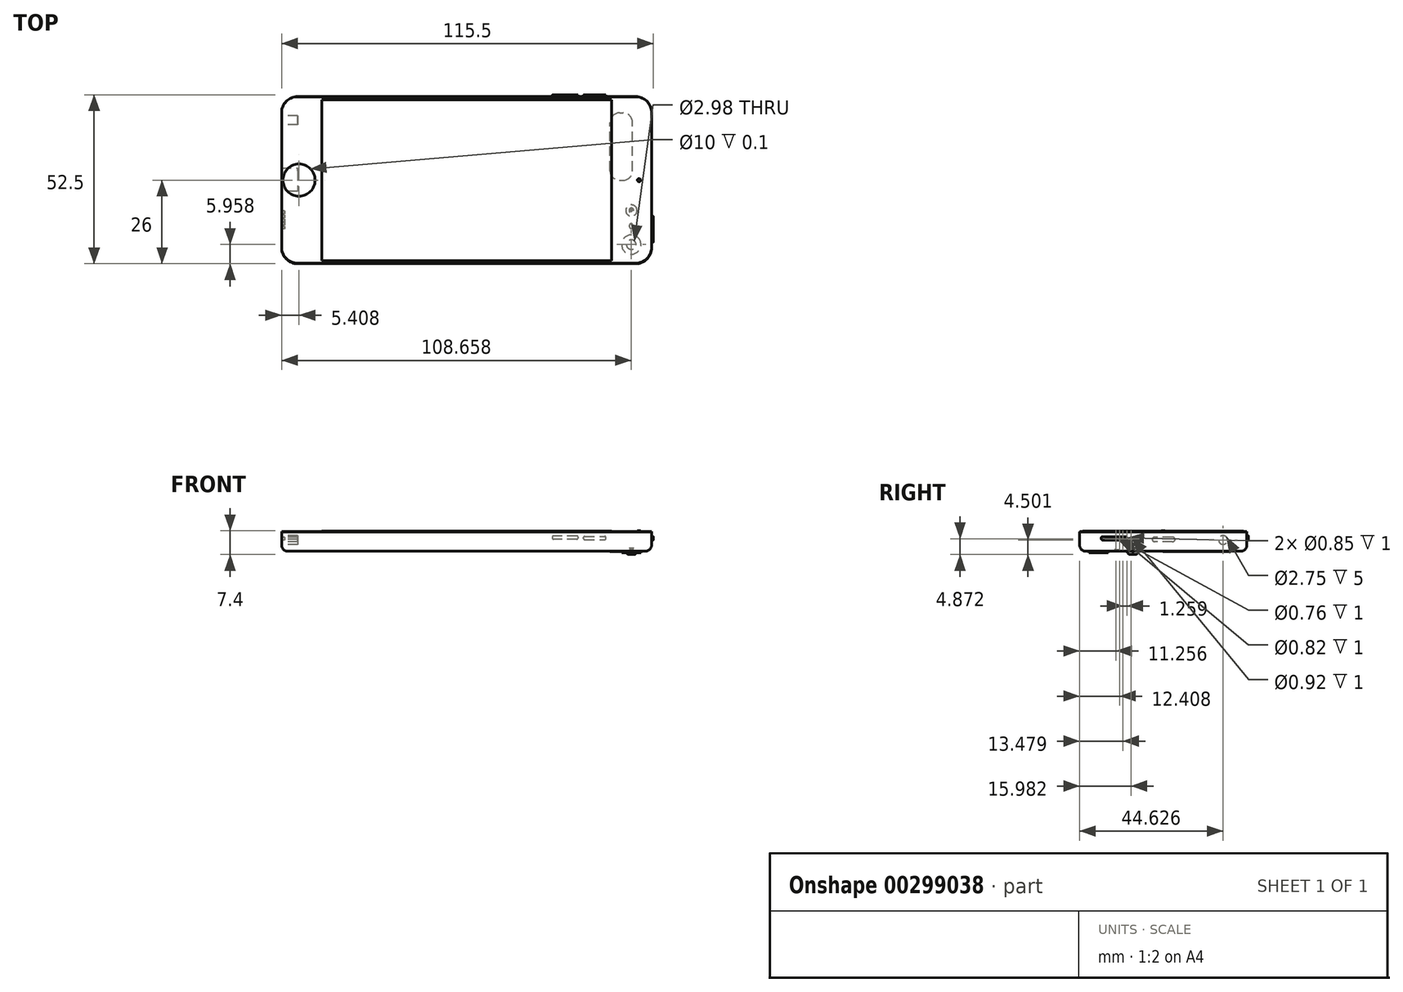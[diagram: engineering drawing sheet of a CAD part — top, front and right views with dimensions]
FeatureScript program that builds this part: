
annotation { "Feature Type Name" : "Feature", "Feature Type Description" : "" }
export const myFeature = defineFeature(function(context is Context, id is Id, definition is map)
    precondition{}
    {
        {
            var Q0;
            Q0=qCreatedBy(makeId("Top.planeOp"),FACE);
            var sketch = newSketch(context, id + "F0", { "sketchPlane" : qUnion([Q0])});
            skLineSegment(sketch, "E0.rect.bottom", {"start": v(-57.5, 26) * mm, "end": v(57.5, 26) * mm});
            skLineSegment(sketch, "E0.rect.top", {"start": v(-57.5, -26) * mm, "end": v(57.5, -26) * mm});
            skLineSegment(sketch, "E0.rect.left", {"start": v(-57.5, 26) * mm, "end": v(-57.5, -26) * mm});
            skLineSegment(sketch, "E0.rect.right", {"start": v(57.5, 26) * mm, "end": v(57.5, -26) * mm});
            skPoint(sketch, "E0.rect.middle", {"position": v(0, 0) * mm});
            skSolve(sketch);
        }
        {
            var Q0;
            Q0=makeQuery(id+"F0.imprint","IMPRINT",FACE,{"disambiguationData":[TD([[makeQuery(id+"F0.imprint","IMPRINT",EDGE,{"derivedFrom":sQuery(id+"F0.wireOp",EDGE,"E0.rect.bottom")}),-1.0]])]});
            extrude(context, id + "F1", {"entities" : qUnion([Q0]), "depth" : 6 * mm});
        }
        {
            var Q0;
            Q0=makeQuery(id+"F1.opExtrude","SWEPT_EDGE",EDGE,{"disambiguationData":[OSD([sQuery(id+"F0.wireOp",EDGE,"E0.rect.bottom"),sQuery(id+"F0.wireOp",EDGE,"E0.rect.right")])]});
            fillet(context, id + "F2", {"entities" : qUnion([Q0]), "radius" : 5 * mm, "tangentPropagation" : true, "allowEdgeOverflow" : false});
        }
        {
            var Q0;
            Q0=makeQuery(id+"F1.opExtrude","SWEPT_EDGE",EDGE,{"disambiguationData":[OSD([sQuery(id+"F0.wireOp",EDGE,"E0.rect.top"),sQuery(id+"F0.wireOp",EDGE,"E0.rect.right")])]});
            fillet(context, id + "F3", {"entities" : qUnion([Q0]), "radius" : 5 * mm, "tangentPropagation" : true, "allowEdgeOverflow" : false});
        }
        {
            var Q0;
            Q0=makeQuery(id+"F1.opExtrude","SWEPT_EDGE",EDGE,{"disambiguationData":[OSD([sQuery(id+"F0.wireOp",EDGE,"E0.rect.top"),sQuery(id+"F0.wireOp",EDGE,"E0.rect.left")])]});
            fillet(context, id + "F4", {"entities" : qUnion([Q0]), "radius" : 5 * mm, "tangentPropagation" : true, "allowEdgeOverflow" : false});
        }
        {
            var Q0;
            Q0=makeQuery(id+"F1.opExtrude","SWEPT_EDGE",EDGE,{"disambiguationData":[OSD([sQuery(id+"F0.wireOp",EDGE,"E0.rect.bottom"),sQuery(id+"F0.wireOp",EDGE,"E0.rect.left")])]});
            fillet(context, id + "F5", {"entities" : qUnion([Q0]), "radius" : 5 * mm, "tangentPropagation" : true, "allowEdgeOverflow" : false});
        }
        {
            var Q0;
            Q0=makeQuery(id+"F1.opExtrude","CAP_EDGE",EDGE,{"disambiguationData":[OSD([sQuery(id+"F0.wireOp",EDGE,"E0.rect.top")])],"isStart":true});
            fillet(context, id + "F6", {"entities" : qUnion([Q0]), "radius" : 2 * mm, "tangentPropagation" : true, "allowEdgeOverflow" : false});
        }
        {
            var Q0;
            Q0=makeQuery(id+"F1.opExtrude","SWEPT_FACE",FACE,{"disambiguationData":[OSD([sQuery(id+"F0.wireOp",EDGE,"E0.rect.bottom")])]});
            var sketch = newSketch(context, id + "F7", { "sketchPlane" : qUnion([Q0])});
            skLineSegment(sketch, "E1.right", {"start": v(-43.3, 3.62) * mm, "end": v(-43.3, 4.62) * mm});
            skLineSegment(sketch, "E2.0.MirrorCS", {"start": v(-36.3, 4.62) * mm, "end": v(-43.3, 4.62) * mm});
            skLineSegment(sketch, "E3.0.MirrorCS", {"start": v(-36.3, 3.62) * mm, "end": v(-36.3, 4.62) * mm});
            skLineSegment(sketch, "E4.0.MirrorCS", {"start": v(-36.3, 3.62) * mm, "end": v(-43.3, 3.62) * mm});
            skSolve(sketch);
        }
        {
            var Q0;
            Q0=qSketchRegion(id+"F7",true);
            extrude(context, id + "F8", {"entities" : qUnion([Q0]), "operationType" : NewBodyOperationType.ADD, "depth" : .5 * mm});
        }
        {
            var Q0;
            Q0=makeQuery(id+"F8.opExtrude","SWEPT_EDGE",EDGE,{"disambiguationData":[OSD([sQuery(id+"F7.wireOp",EDGE,"E1.right"),sQuery(id+"F7.wireOp",EDGE,"E2.0.MirrorCS")])]});
            var Q1;
            Q1=makeQuery(id+"F8.opExtrude","SWEPT_EDGE",EDGE,{"disambiguationData":[OSD([sQuery(id+"F7.wireOp",EDGE,"E1.right"),sQuery(id+"F7.wireOp",EDGE,"E4.0.MirrorCS")])]});
            var Q2;
            Q2=makeQuery(id+"F8.opExtrude","SWEPT_EDGE",EDGE,{"disambiguationData":[OSD([sQuery(id+"F7.wireOp",EDGE,"E3.0.MirrorCS"),sQuery(id+"F7.wireOp",EDGE,"E4.0.MirrorCS")])]});
            var Q3;
            Q3=makeQuery(id+"F8.opExtrude","SWEPT_EDGE",EDGE,{"disambiguationData":[OSD([sQuery(id+"F7.wireOp",EDGE,"E2.0.MirrorCS"),sQuery(id+"F7.wireOp",EDGE,"E3.0.MirrorCS")])]});
            fillet(context, id + "F9", {"entities" : qUnion([Q0, Q1, Q2, Q3]), "radius" : .4 * mm, "tangentPropagation" : true, "allowEdgeOverflow" : false});
        }
        {
            var Q0;
            Q0=makeQuery(id+"F1.opExtrude","SWEPT_FACE",FACE,{"disambiguationData":[OSD([sQuery(id+"F0.wireOp",EDGE,"E0.rect.bottom")])]});
            var sketch = newSketch(context, id + "F10", { "sketchPlane" : qUnion([Q0])});
            skLineSegment(sketch, "E5.bottom", {"start": v(-34.62, 4.76) * mm, "end": v(-26.62, 4.76) * mm});
            skLineSegment(sketch, "E5.top", {"start": v(-34.62, 3.76) * mm, "end": v(-26.62, 3.76) * mm});
            skLineSegment(sketch, "E5.left", {"start": v(-34.62, 4.76) * mm, "end": v(-34.62, 3.76) * mm});
            skLineSegment(sketch, "E5.right", {"start": v(-26.62, 4.76) * mm, "end": v(-26.62, 3.76) * mm});
            skSolve(sketch);
        }
        {
            var Q0;
            Q0=qSketchRegion(id+"F10",true);
            extrude(context, id + "F11", {"entities" : qUnion([Q0]), "operationType" : NewBodyOperationType.ADD, "depth" : .5 * mm});
        }
        {
            var Q0;
            Q0=makeQuery(id+"F11.opExtrude","SWEPT_EDGE",EDGE,{"disambiguationData":[OSD([sQuery(id+"F10.wireOp",EDGE,"E5.bottom"),sQuery(id+"F10.wireOp",EDGE,"E5.left")])]});
            var Q1;
            Q1=makeQuery(id+"F11.opExtrude","SWEPT_EDGE",EDGE,{"disambiguationData":[OSD([sQuery(id+"F10.wireOp",EDGE,"E5.top"),sQuery(id+"F10.wireOp",EDGE,"E5.left")])]});
            var Q2;
            Q2=makeQuery(id+"F11.opExtrude","SWEPT_EDGE",EDGE,{"disambiguationData":[OSD([sQuery(id+"F10.wireOp",EDGE,"E5.top"),sQuery(id+"F10.wireOp",EDGE,"E5.right")])]});
            var Q3;
            Q3=makeQuery(id+"F11.opExtrude","SWEPT_EDGE",EDGE,{"disambiguationData":[OSD([sQuery(id+"F10.wireOp",EDGE,"E5.bottom"),sQuery(id+"F10.wireOp",EDGE,"E5.right")])]});
            fillet(context, id + "F12", {"entities" : qUnion([Q0, Q1, Q2, Q3]), "radius" : .4 * mm, "tangentPropagation" : true, "allowEdgeOverflow" : false});
        }
        {
            var Q0;
            Q0=makeQuery(id+"F1.opExtrude","SWEPT_FACE",FACE,{"disambiguationData":[OSD([sQuery(id+"F0.wireOp",EDGE,"E0.rect.left")])]});
            var sketch = newSketch(context, id + "F13", { "sketchPlane" : qUnion([Q0])});
            skCircle(sketch, "E6", {"center": v(-18.63, 3.5) * mm, "radius": 1.38 * mm});
            skSolve(sketch);
        }
        {
            var Q0;
            Q0=qSketchRegion(id+"F13",true);
            extrude(context, id + "F14", {"entities" : qUnion([Q0]), "operationType" : NewBodyOperationType.REMOVE, "oppositeDirection" : true, "depth" : 5 * mm});
        }
        {
            var Q0;
            Q0=makeQuery(id+"F1.opExtrude","SWEPT_FACE",FACE,{"disambiguationData":[OSD([sQuery(id+"F0.wireOp",EDGE,"E0.rect.left")])]});
            var sketch = newSketch(context, id + "F15", { "sketchPlane" : qUnion([Q0])});
            skLineSegment(sketch, "E7.bottom", {"start": v(-3.75, 4.39) * mm, "end": v(3.47, 4.39) * mm});
            skLineSegment(sketch, "E7.top", {"start": v(-3.75, 2.97) * mm, "end": v(3.47, 2.97) * mm});
            skLineSegment(sketch, "E7.left", {"start": v(-3.75, 4.39) * mm, "end": v(-3.75, 2.97) * mm});
            skLineSegment(sketch, "E7.right", {"start": v(3.47, 4.39) * mm, "end": v(3.47, 2.97) * mm});
            skSolve(sketch);
        }
        {
            var Q0;
            Q0=makeQuery(id+"F15.imprint","IMPRINT",FACE,{"disambiguationData":[TD([[makeQuery(id+"F15.imprint","IMPRINT",EDGE,{"derivedFrom":sQuery(id+"F15.wireOp",EDGE,"E7.bottom")}),-1.0]])]});
            extrude(context, id + "F16", {"entities" : qUnion([Q0]), "operationType" : NewBodyOperationType.REMOVE, "oppositeDirection" : true, "depth" : 5 * mm});
        }
        {
            var Q0;
            Q0=makeQuery(id+"F16.boolean.opBoolean","COPY",EDGE,{"derivedFrom":makeQuery(id+"F16.opExtrude","SWEPT_EDGE",EDGE,{"disambiguationData":[OSD([sQuery(id+"F15.wireOp",EDGE,"E7.bottom"),sQuery(id+"F15.wireOp",EDGE,"E7.left")])]})});
            var Q1;
            Q1=makeQuery(id+"F16.boolean.opBoolean","COPY",EDGE,{"derivedFrom":makeQuery(id+"F16.opExtrude","SWEPT_EDGE",EDGE,{"disambiguationData":[OSD([sQuery(id+"F15.wireOp",EDGE,"E7.top"),sQuery(id+"F15.wireOp",EDGE,"E7.left")])]})});
            var Q2;
            Q2=makeQuery(id+"F16.boolean.opBoolean","COPY",EDGE,{"derivedFrom":makeQuery(id+"F16.opExtrude","SWEPT_EDGE",EDGE,{"disambiguationData":[OSD([sQuery(id+"F15.wireOp",EDGE,"E7.bottom"),sQuery(id+"F15.wireOp",EDGE,"E7.right")])]})});
            var Q3;
            Q3=makeQuery(id+"F16.boolean.opBoolean","COPY",EDGE,{"derivedFrom":makeQuery(id+"F16.opExtrude","SWEPT_EDGE",EDGE,{"disambiguationData":[OSD([sQuery(id+"F15.wireOp",EDGE,"E7.top"),sQuery(id+"F15.wireOp",EDGE,"E7.right")])]})});
            fillet(context, id + "F17", {"entities" : qUnion([Q0, Q1, Q2, Q3]), "radius" : .9 * mm, "tangentPropagation" : true, "allowEdgeOverflow" : false});
        }
        {
            var Q0;
            Q0=makeQuery(id+"F1.opExtrude","SWEPT_FACE",FACE,{"disambiguationData":[OSD([sQuery(id+"F0.wireOp",EDGE,"E0.rect.left")])]});
            var sketch = newSketch(context, id + "F18", { "sketchPlane" : qUnion([Q0])});
            skCircle(sketch, "E8", {"center": v(10.02, 3.87) * mm, "radius": 0.46 * mm});
            skCircle(sketch, "E9", {"center": v(11.26, 3.87) * mm, "radius": 0.42 * mm});
            skCircle(sketch, "E10", {"center": v(12.52, 3.87) * mm, "radius": 0.42 * mm});
            skCircle(sketch, "E11", {"center": v(13.6, 3.87) * mm, "radius": 0.41 * mm});
            skCircle(sketch, "E12", {"center": v(14.74, 3.87) * mm, "radius": 0.38 * mm});
            skSolve(sketch);
        }
        {
            var Q0;
            Q0=qSketchRegion(id+"F18",true);
            extrude(context, id + "F19", {"entities" : qUnion([Q0]), "operationType" : NewBodyOperationType.REMOVE, "oppositeDirection" : true, "depth" : 1 * mm});
        }
        {
            var Q0;
            Q0=makeQuery(id+"F1.opExtrude","SWEPT_FACE",FACE,{"disambiguationData":[OSD([sQuery(id+"F0.wireOp",EDGE,"E0.rect.right")])]});
            var sketch = newSketch(context, id + "F20", { "sketchPlane" : qUnion([Q0])});
            skLineSegment(sketch, "E13.bottom", {"start": v(-19.26, 4.51) * mm, "end": v(-11.26, 4.51) * mm});
            skLineSegment(sketch, "E13.top", {"start": v(-19.26, 3.51) * mm, "end": v(-11.26, 3.51) * mm});
            skLineSegment(sketch, "E13.left", {"start": v(-19.26, 4.51) * mm, "end": v(-19.26, 3.51) * mm});
            skLineSegment(sketch, "E13.right", {"start": v(-11.26, 4.51) * mm, "end": v(-11.26, 3.51) * mm});
            skSolve(sketch);
        }
        {
            var Q0;
            Q0=makeQuery(id+"F20.imprint","IMPRINT",FACE,{"disambiguationData":[TD([[makeQuery(id+"F20.imprint","IMPRINT",EDGE,{"derivedFrom":sQuery(id+"F20.wireOp",EDGE,"E13.bottom")}),-1.0]])]});
            extrude(context, id + "F21", {"entities" : qUnion([Q0]), "operationType" : NewBodyOperationType.ADD, "depth" : .5 * mm});
        }
        {
            var Q0;
            Q0=makeQuery(id+"F21.opExtrude","SWEPT_EDGE",EDGE,{"disambiguationData":[OSD([sQuery(id+"F20.wireOp",EDGE,"E13.bottom"),sQuery(id+"F20.wireOp",EDGE,"E13.left")])]});
            var Q1;
            Q1=makeQuery(id+"F21.opExtrude","SWEPT_EDGE",EDGE,{"disambiguationData":[OSD([sQuery(id+"F20.wireOp",EDGE,"E13.top"),sQuery(id+"F20.wireOp",EDGE,"E13.left")])]});
            var Q2;
            Q2=makeQuery(id+"F21.opExtrude","SWEPT_EDGE",EDGE,{"disambiguationData":[OSD([sQuery(id+"F20.wireOp",EDGE,"E13.bottom"),sQuery(id+"F20.wireOp",EDGE,"E13.right")])]});
            var Q3;
            Q3=makeQuery(id+"F21.opExtrude","SWEPT_EDGE",EDGE,{"disambiguationData":[OSD([sQuery(id+"F20.wireOp",EDGE,"E13.top"),sQuery(id+"F20.wireOp",EDGE,"E13.right")])]});
            fillet(context, id + "F22", {"entities" : qUnion([Q0, Q1, Q2, Q3]), "radius" : .4 * mm, "tangentPropagation" : true, "allowEdgeOverflow" : false});
        }
        {
            var Q0;
            Q0=makeQuery(id+"F1.opExtrude","CAP_FACE",FACE,{"disambiguationData":[OSD([sQuery(id+"F0.wireOp",EDGE,"E0.rect.bottom"),sQuery(id+"F0.wireOp",EDGE,"E0.rect.top"),sQuery(id+"F0.wireOp",EDGE,"E0.rect.left"),sQuery(id+"F0.wireOp",EDGE,"E0.rect.right")])],"isStart":true});
            var sketch = newSketch(context, id + "F23", { "sketchPlane" : qUnion([Q0])});
            skCircle(sketch, "E14", {"center": v(51.16, 20.04) * mm, "radius": 3 * mm});
            skCircle(sketch, "E15", {"center": v(51.16, 20.04) * mm, "radius": 1.5 * mm});
            skSolve(sketch);
        }
        {
            var Q0;
            Q0=makeQuery(id+"F23.imprint","IMPRINT",FACE,{"disambiguationData":[TD([[makeQuery(id+"F23.imprint","IMPRINT",EDGE,{"derivedFrom":sQuery(id+"F23.wireOp",EDGE,"E14")}),1.0]])]});
            extrude(context, id + "F24", {"entities" : qUnion([Q0]), "depth" : .5 * mm});
        }
        {
            var Q0;
            Q0=makeQuery(id+"F1.opExtrude","CAP_FACE",FACE,{"disambiguationData":[OSD([sQuery(id+"F0.wireOp",EDGE,"E0.rect.bottom"),sQuery(id+"F0.wireOp",EDGE,"E0.rect.top"),sQuery(id+"F0.wireOp",EDGE,"E0.rect.left"),sQuery(id+"F0.wireOp",EDGE,"E0.rect.right")])],"isStart":true});
            var sketch = newSketch(context, id + "F25", { "sketchPlane" : qUnion([Q0])});
            skLineSegment(sketch, "E16.rect.bottom", {"start": v(50.61, 15.04) * mm, "end": v(51.61, 15.04) * mm});
            skLineSegment(sketch, "E16.rect.top", {"start": v(50.61, 13.54) * mm, "end": v(51.61, 13.54) * mm});
            skLineSegment(sketch, "E16.rect.left", {"start": v(50.61, 15.04) * mm, "end": v(50.61, 13.54) * mm});
            skLineSegment(sketch, "E16.rect.right", {"start": v(51.61, 15.04) * mm, "end": v(51.61, 13.54) * mm});
            skPoint(sketch, "E16.rect.middle", {"position": v(51.11, 14.3) * mm});
            skSolve(sketch);
        }
        {
            var Q0;
            Q0=qSketchRegion(id+"F25",true);
            extrude(context, id + "F26", {"entities" : qUnion([Q0]), "operationType" : NewBodyOperationType.REMOVE, "oppositeDirection" : true, "depth" : .5 * mm});
        }
        {
            var Q0;
            Q0=makeQuery(id+"F26.boolean.opBoolean","COPY",EDGE,{"derivedFrom":makeQuery(id+"F26.opExtrude","SWEPT_EDGE",EDGE,{"disambiguationData":[OSD([sQuery(id+"F25.wireOp",EDGE,"E16.rect.top"),sQuery(id+"F25.wireOp",EDGE,"E16.rect.left")])]})});
            var Q1;
            Q1=makeQuery(id+"F26.boolean.opBoolean","COPY",EDGE,{"derivedFrom":makeQuery(id+"F26.opExtrude","SWEPT_EDGE",EDGE,{"disambiguationData":[OSD([sQuery(id+"F25.wireOp",EDGE,"E16.rect.bottom"),sQuery(id+"F25.wireOp",EDGE,"E16.rect.left")])]})});
            var Q2;
            Q2=makeQuery(id+"F26.boolean.opBoolean","COPY",EDGE,{"derivedFrom":makeQuery(id+"F26.opExtrude","SWEPT_EDGE",EDGE,{"disambiguationData":[OSD([sQuery(id+"F25.wireOp",EDGE,"E16.rect.bottom"),sQuery(id+"F25.wireOp",EDGE,"E16.rect.right")])]})});
            var Q3;
            Q3=makeQuery(id+"F26.boolean.opBoolean","COPY",EDGE,{"derivedFrom":makeQuery(id+"F26.opExtrude","SWEPT_EDGE",EDGE,{"disambiguationData":[OSD([sQuery(id+"F25.wireOp",EDGE,"E16.rect.top"),sQuery(id+"F25.wireOp",EDGE,"E16.rect.right")])]})});
            fillet(context, id + "F27", {"entities" : qUnion([Q0, Q1, Q2, Q3]), "radius" : .5 * mm, "tangentPropagation" : true, "allowEdgeOverflow" : false});
        }
        {
            var Q0;
            Q0=makeQuery(id+"F1.opExtrude","CAP_FACE",FACE,{"disambiguationData":[OSD([sQuery(id+"F0.wireOp",EDGE,"E0.rect.bottom"),sQuery(id+"F0.wireOp",EDGE,"E0.rect.top"),sQuery(id+"F0.wireOp",EDGE,"E0.rect.left"),sQuery(id+"F0.wireOp",EDGE,"E0.rect.right")])],"isStart":true});
            var sketch = newSketch(context, id + "F28", { "sketchPlane" : qUnion([Q0])});
            skCircle(sketch, "E17", {"center": v(51.2, 9.45) * mm, "radius": 1.75 * mm});
            skSolve(sketch);
        }
        {
            var Q0;
            Q0=qSketchRegion(id+"F28",true);
            extrude(context, id + "F29", {"entities" : qUnion([Q0]), "operationType" : NewBodyOperationType.REMOVE, "oppositeDirection" : true, "depth" : 1 * mm});
        }
        {
            var Q0;
            Q0=makeQuery(id+"F29.boolean.opBoolean","COPY",EDGE,{"derivedFrom":makeQuery(id+"F29.opExtrude","CAP_EDGE",EDGE,{"disambiguationData":[OSD([sQuery(id+"F28.wireOp",EDGE,"E17")])],"isStart":false})});
            fillet(context, id + "F30", {"entities" : qUnion([Q0]), "radius" : 1 * mm, "tangentPropagation" : true, "allowEdgeOverflow" : false});
        }
        {
            var Q0;
            Q0=makeQuery(id+"F1.opExtrude","CAP_FACE",FACE,{"disambiguationData":[OSD([sQuery(id+"F0.wireOp",EDGE,"E0.rect.bottom"),sQuery(id+"F0.wireOp",EDGE,"E0.rect.top"),sQuery(id+"F0.wireOp",EDGE,"E0.rect.left"),sQuery(id+"F0.wireOp",EDGE,"E0.rect.right")])],"isStart":true});
            var sketch = newSketch(context, id + "F31", { "sketchPlane" : qUnion([Q0])});
            skLineSegment(sketch, "E18.rect.bottom", {"start": v(44.56, 0.08) * mm, "end": v(51.56, 0.08) * mm});
            skLineSegment(sketch, "E18.rect.top", {"start": v(44.56, -20.92) * mm, "end": v(51.56, -20.92) * mm});
            skLineSegment(sketch, "E18.rect.left", {"start": v(44.56, 0.08) * mm, "end": v(44.56, -20.92) * mm});
            skLineSegment(sketch, "E18.rect.right", {"start": v(51.56, 0.08) * mm, "end": v(51.56, -20.92) * mm});
            skPoint(sketch, "E18.rect.middle", {"position": v(48.06, -10.42) * mm});
            skSolve(sketch);
        }
        {
            var Q0;
            Q0=makeQuery(id+"F31.imprint","IMPRINT",FACE,{"disambiguationData":[TD([[makeQuery(id+"F31.imprint","IMPRINT",EDGE,{"derivedFrom":sQuery(id+"F31.wireOp",EDGE,"E18.rect.bottom")}),-1.0]])]});
            var Q1;
            Q1=sQuery(id+"F31.wireOp",EDGE,"E18.rect.right");
            extrude(context, id + "F32", {"entities" : qUnion([Q0]), "surfaceEntities" : qUnion([Q1]), "depth" : 0.1 * mm});
        }
        {
            var Q0;
            Q0=makeQuery(id+"F32.opExtrude","SWEPT_EDGE",EDGE,{"disambiguationData":[OSD([sQuery(id+"F31.wireOp",EDGE,"E18.rect.top"),sQuery(id+"F31.wireOp",EDGE,"E18.rect.right")])]});
            var Q1;
            Q1=makeQuery(id+"F32.opExtrude","SWEPT_EDGE",EDGE,{"disambiguationData":[OSD([sQuery(id+"F31.wireOp",EDGE,"E18.rect.top"),sQuery(id+"F31.wireOp",EDGE,"E18.rect.left")])]});
            var Q2;
            Q2=makeQuery(id+"F32.opExtrude","SWEPT_EDGE",EDGE,{"disambiguationData":[OSD([sQuery(id+"F31.wireOp",EDGE,"E18.rect.bottom"),sQuery(id+"F31.wireOp",EDGE,"E18.rect.right")])]});
            var Q3;
            Q3=makeQuery(id+"F32.opExtrude","SWEPT_EDGE",EDGE,{"disambiguationData":[OSD([sQuery(id+"F31.wireOp",EDGE,"E18.rect.bottom"),sQuery(id+"F31.wireOp",EDGE,"E18.rect.left")])]});
            fillet(context, id + "F33", {"entities" : qUnion([Q0, Q1, Q2, Q3]), "radius" : 3 * mm, "tangentPropagation" : true, "allowEdgeOverflow" : false});
        }
        {
            var Q0;
            Q0=makeQuery(id+"F1.opExtrude","CAP_FACE",FACE,{"disambiguationData":[OSD([sQuery(id+"F0.wireOp",EDGE,"E0.rect.bottom"),sQuery(id+"F0.wireOp",EDGE,"E0.rect.top"),sQuery(id+"F0.wireOp",EDGE,"E0.rect.left"),sQuery(id+"F0.wireOp",EDGE,"E0.rect.right")])],"isStart":false});
            var sketch = newSketch(context, id + "F34", { "sketchPlane" : qUnion([Q0])});
            skLineSegment(sketch, "E19.bottom", {"start": v(57.5, -25.82) * mm, "end": v(-57.5, -25.82) * mm});
            skLineSegment(sketch, "E19.top", {"start": v(57.5, 25.93) * mm, "end": v(-57.5, 25.93) * mm});
            skLineSegment(sketch, "E19.left", {"start": v(57.5, -25.82) * mm, "end": v(57.5, 25.93) * mm});
            skLineSegment(sketch, "E19.right", {"start": v(-57.5, -25.82) * mm, "end": v(-57.5, 25.93) * mm});
            skSolve(sketch);
        }
        {
            var Q0;
            Q0=qSketchRegion(id+"F34",true);
            extrude(context, id + "F35", {"entities" : qUnion([Q0]), "depth" : 0.2 * mm});
        }
        {
            var Q0;
            Q0=makeQuery(id+"F35.opExtrude","SWEPT_EDGE",EDGE,{"disambiguationData":[OSD([sQuery(id+"F34.wireOp",EDGE,"E19.top"),sQuery(id+"F34.wireOp",EDGE,"E19.right")])]});
            var Q1;
            Q1=makeQuery(id+"F35.opExtrude","SWEPT_EDGE",EDGE,{"disambiguationData":[OSD([sQuery(id+"F34.wireOp",EDGE,"E19.top"),sQuery(id+"F34.wireOp",EDGE,"E19.left")])]});
            var Q2;
            Q2=makeQuery(id+"F35.opExtrude","SWEPT_EDGE",EDGE,{"disambiguationData":[OSD([sQuery(id+"F34.wireOp",EDGE,"E19.bottom"),sQuery(id+"F34.wireOp",EDGE,"E19.left")])]});
            var Q3;
            Q3=makeQuery(id+"F35.opExtrude","SWEPT_EDGE",EDGE,{"disambiguationData":[OSD([sQuery(id+"F34.wireOp",EDGE,"E19.bottom"),sQuery(id+"F34.wireOp",EDGE,"E19.right")])]});
            fillet(context, id + "F36", {"entities" : qUnion([Q0, Q1, Q2, Q3]), "radius" : 5 * mm, "tangentPropagation" : true, "allowEdgeOverflow" : false});
        }
        {
            var Q0;
            Q0=makeQuery(id+"F35.opExtrude","CAP_FACE",FACE,{"disambiguationData":[OSD([sQuery(id+"F34.wireOp",EDGE,"E19.bottom"),sQuery(id+"F34.wireOp",EDGE,"E19.top"),sQuery(id+"F34.wireOp",EDGE,"E19.left"),sQuery(id+"F34.wireOp",EDGE,"E19.right")])],"isStart":false});
            var sketch = newSketch(context, id + "F37", { "sketchPlane" : qUnion([Q0])});
            skSolve(sketch);
        }
        {
            var Q0;
            {var subQ3=sQuery(id+"F34.wireOp",EDGE,"E19.bottom");Q0=makeQuery(id+"F37.imprint","IMPRINT",FACE,{"disambiguationData":[TD([[makeQuery(id+"F37.imprint","IMPRINT",EDGE,{"derivedFrom":makeQuery(id+"F35.opExtrude","CAP_EDGE",EDGE,{"disambiguationData":[OSD([subQ3])],"isStart":false})}),-1.0]])]});}
            var sketch = newSketch(context, id + "F38", { "sketchPlane" : qUnion([Q0])});
            skCircle(sketch, "E20", {"center": v(53.58, 0) * mm, "radius": 0.5 * mm});
            skSolve(sketch);
        }
        {
            var Q0;
            Q0=qSketchRegion(id+"F38",true);
            extrude(context, id + "F39", {"entities" : qUnion([Q0]), "depth" : 0.2 * mm});
        }
        {
            var Q0;
            {var subQ3=sQuery(id+"F34.wireOp",EDGE,"E19.bottom");Q0=makeQuery(id+"F37.imprint","IMPRINT",FACE,{"disambiguationData":[TD([[makeQuery(id+"F37.imprint","IMPRINT",EDGE,{"derivedFrom":makeQuery(id+"F35.opExtrude","CAP_EDGE",EDGE,{"disambiguationData":[OSD([subQ3])],"isStart":false})}),-1.0]])]});}
            var sketch = newSketch(context, id + "F40", { "sketchPlane" : qUnion([Q0])});
            skLineSegment(sketch, "E21.rect.bottom", {"start": v(-45, 25) * mm, "end": v(45, 25) * mm});
            skLineSegment(sketch, "E21.rect.top", {"start": v(-45, -25) * mm, "end": v(45, -25) * mm});
            skLineSegment(sketch, "E21.rect.left", {"start": v(-45, 25) * mm, "end": v(-45, -25) * mm});
            skLineSegment(sketch, "E21.rect.right", {"start": v(45, 25) * mm, "end": v(45, -25) * mm});
            skPoint(sketch, "E21.rect.middle", {"position": v(0, 0) * mm});
            skSolve(sketch);
        }
        {
            var Q0;
            Q0=qSketchRegion(id+"F40",true);
            extrude(context, id + "F41", {"entities" : qUnion([Q0]), "depth" : 0.1 * mm});
        }
        {
            var Q0;
            {var subQ3=sQuery(id+"F34.wireOp",EDGE,"E19.bottom");Q0=makeQuery(id+"F37.imprint","IMPRINT",FACE,{"disambiguationData":[TD([[makeQuery(id+"F37.imprint","IMPRINT",EDGE,{"derivedFrom":makeQuery(id+"F35.opExtrude","CAP_EDGE",EDGE,{"disambiguationData":[OSD([subQ3])],"isStart":false})}),-1.0]])]});}
            var sketch = newSketch(context, id + "F42", { "sketchPlane" : qUnion([Q0])});
            skCircle(sketch, "E22", {"center": v(-52.1, 0) * mm, "radius": 5 * mm});
            skSolve(sketch);
        }
        {
            var Q0;
            Q0=qSketchRegion(id+"F42",true);
            var Q1;
            Q1=sQuery(id+"F42.wireOp",EDGE,"E22");
            extrude(context, id + "F43", {"entities" : qUnion([Q0]), "operationType" : NewBodyOperationType.REMOVE, "surfaceEntities" : qUnion([Q1]), "oppositeDirection" : true, "depth" : .1 * mm});
        }
    });
